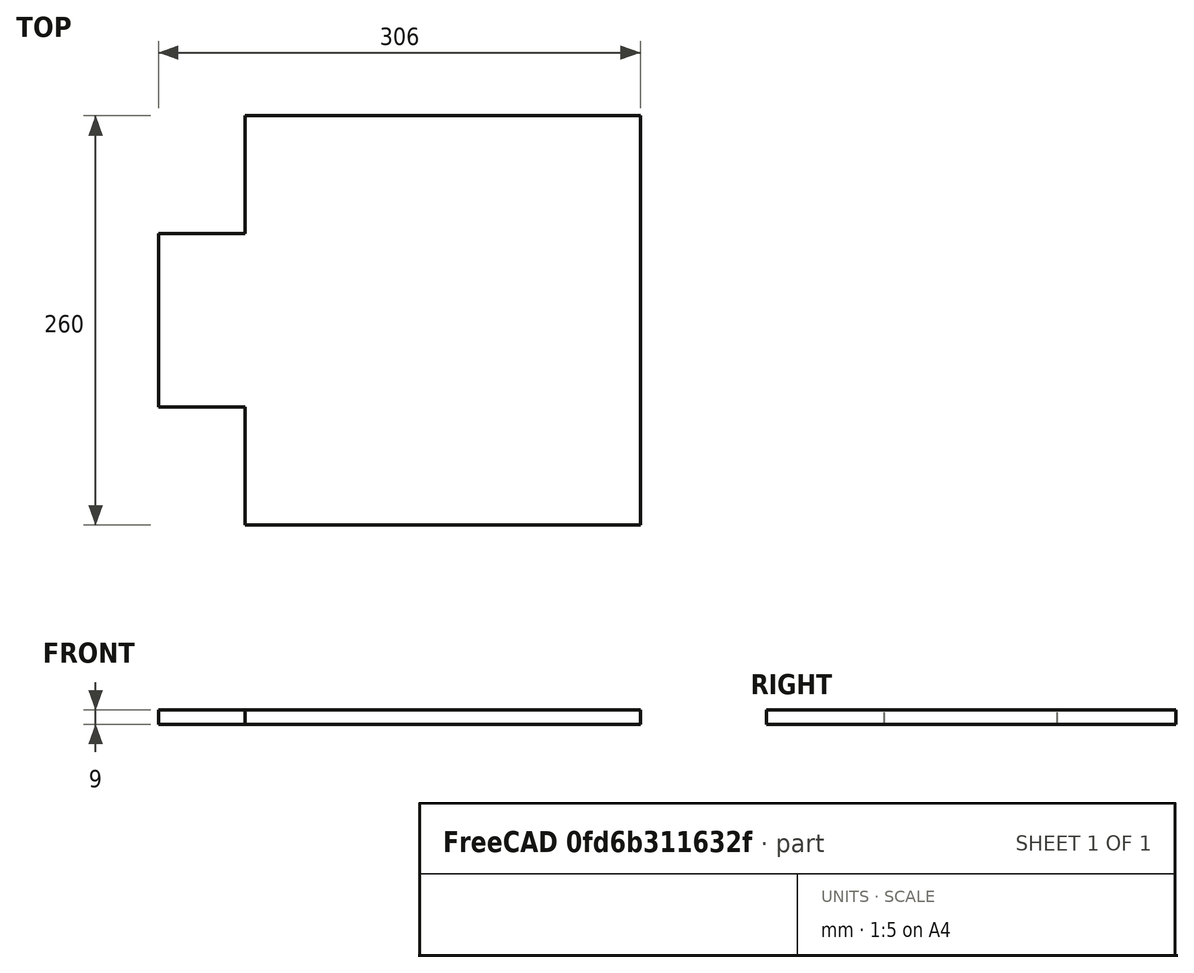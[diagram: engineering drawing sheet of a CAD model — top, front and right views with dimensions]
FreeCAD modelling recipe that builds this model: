
FCSTD DOCUMENT  (FreeCAD 0.16RUnknown)
Label: plaque_ar
License: All rights reserved
LicenseURL: http://en.wikipedia.org/wiki/All_rights_reserved
objects: App::FeaturePython×6, App::DocumentObjectGroup×4, Drawing::FeatureViewPart×4, Part::Plane×3, Drawing::FeatureViewPython×3, Part::Fuse×1, Part::Cut×1, Part::FeaturePython×1, Part::Extrusion×1, Drawing::FeaturePage×1
note: 7 computed .brp shape members not serialized (recipe doc carries the construction recipe); baked Part::Feature solids carry a one-line shape summary decoded from their .brp

FEATURE [Part::Plane] square
  Length = 306
  Placement = pos=(20,-130,0) rot=(0,0,1;0rad)
  Width = 260
FEATURE [Part::Plane] square001
  Length = 75
  Placement = pos=(0,55,0) rot=(0,0,1;0rad)
  Width = 75
FEATURE [Part::Plane] square002
  Length = 75
  Placement = pos=(0,-130,0) rot=(0,0,1;0rad)
  Width = 75
FEATURE [Part::Fuse] union
  Base = -> square001
  Tool = -> square002
FEATURE [Part::Cut] difference
  Base = -> square
  Tool = -> union
FEATURE [Part::FeaturePython] RefineLinearExtrude  # WARN: FeaturePython — macro-defined, semantics opaque (R4)
  Base = -> difference
FEATURE [Part::Extrusion] LinearExtrude
  Base = -> RefineLinearExtrude
  Dir = (0,0,9)
  Solid = true
FEATURE [App::FeaturePython] Dimension  # Draft dimension (typed FeaturePython)
  Dimline = (332,0,0)
  Direction = (0,0,0)
  Distance = 260
  End = (326,-130,0)
  Normal = (0,0,1)
  Start = (326,130,0)
FEATURE [App::FeaturePython] Dimension001  # Draft dimension (typed FeaturePython)
  Dimline = (0,-136,0)
  Direction = (0,0,0)
  Distance = 306
  End = (326,-130,0)
  Normal = (0,0,1)
  Start = (20,-130,0)
FEATURE [App::DocumentObjectGroup] Groupe001  label="XY"
  Group = -> [Dimension,Dimension001]
FEATURE [App::FeaturePython] Dimension002  # Draft dimension (typed FeaturePython)
  Dimline = (0,0,15)
  Direction = (0,0,0)
  Distance = 55
  End = (75,0,9)
  Normal = (0,-1,-1.19209e-07)
  Start = (20,0,9)
FEATURE [App::FeaturePython] Dimension003  # Draft dimension (typed FeaturePython)
  Dimline = (0,0,15)
  Direction = (0,0,0)
  Distance = 251
  End = (326,0,0)
  Normal = (0,-1,-1.19209e-07)
  Start = (75,0,0)
FEATURE [App::DocumentObjectGroup] Groupe002  label="XZ"
  Group = -> [Dimension002,Dimension003]
FEATURE [App::FeaturePython] Dimension004  # Draft dimension (typed FeaturePython)
  Dimline = (0,0,15)
  Direction = (0,0,0)
  Distance = 75
  End = (0,55,9)
  Normal = (-1,0,0)
  Start = (0,130,9)
FEATURE [App::FeaturePython] Dimension005  # Draft dimension (typed FeaturePython)
  Dimline = (0,0,15)
  Direction = (0,0,0)
  Distance = 110
  End = (0,-55,9)
  Normal = (-1,0,0)
  Start = (0,55,9)
FEATURE [App::DocumentObjectGroup] Groupe003  label="YZ"
  Group = -> [Dimension004,Dimension005]
FEATURE [App::DocumentObjectGroup] Groupe  label="Dimmensions"
  Group = -> [Groupe001,Groupe002,Groupe003]
FEATURE [Drawing::FeatureViewPython] ViewGroupe001  # drawing view (typed FeaturePython)
  Direction = (0,0,0)
  FillStyle = 0
  FontSize = 12
  LineStyle = 0
  LineWidth = 0.35
  Rotation = 90
  Scale = 0.38
  Source = -> Groupe001
  ViewResult = <blob: 2051 chars omitted>
  Visible = true
  X = 150
  Y = 71.79
FEATURE [Drawing::FeatureViewPython] ViewGroupe002  # drawing view (typed FeaturePython)
  Direction = (0,0,0)
  FillStyle = 0
  FontSize = 12
  LineStyle = 0
  LineWidth = 0.35
  Rotation = 90
  Scale = 0.38
  Source = -> Groupe002
  ViewResult = <blob: 2024 chars omitted>
  Visible = true
  X = 44.5
  Y = 71.79
FEATURE [Drawing::FeatureViewPython] ViewGroupe003  # drawing view (typed FeaturePython)
  Direction = (0,0,0)
  FillStyle = 0
  FontSize = 12
  LineStyle = 0
  LineWidth = 0.35
  Rotation = -90
  Scale = 0.38
  Source = -> Groupe003
  ViewResult = <g id="ViewGroupe003" transform="rotate(-90.0,150.0,44.33) translate(150.0,44.33) scale(0.38,-0.38)"><path d="M 0.0 130.0 L 0.0 130.0 L 0.0 55.0 L 0.0 55.0" fill="none" stroke="#000000" stroke-width="0.921052631579 px" style="stroke-width:0.921052631579;stroke-miterlimit:4;stroke-dasharray:none" freecad:basepoint1="0.0 130.0" freecad:basepoint2="0.0 55.0" freecad:dimpoint="0.0 130.0"/>\n<path transform="rotate(-90.0,0.0,130.0) translate(0.0,130.0) scale(0.666666666667,0.666666666667)" freecad:skip="1" fill="#000000" stroke="none" style="stroke-miterlimit:4;stroke-dasharray:none" d="M 0 0 L 4 1 L 4 -1 Z"/>\n<path transform="rotate(90.0,0.0,55.0) translate(0.0,55.0) scale(0.666666666667,0.666666666667)" freecad:skip="1" fill="#000000" stroke="none" style="stroke-miterlimit:4;stroke-dasharray:none" d="M 0 0 L 4 1 L 4 -1 Z"/>\n<text fill="#000000" font-size="15.7894736842" style="text-anchor:middle;text-align:center;font-family:" transform="rotate(-90.0,0.0,92.5) translate(0.0,92.5) scale(1,-1) " freecad:skip="1">\n75,00 </text>\n<path d="M 0.0 55.0 L 0.0 55.0 L 0.0 -55.0 L 0.0 -55.0" fill="none" stroke="#000000" stroke-width="0.921052631579 px" style="stroke-width:0.921052631579;stroke-miterlimit:4;stroke-dasharray:none" freecad:basepoint1="0.0 55.0" freecad:basepoint2="0.0 -55.0" freecad:dimpoint="0.0 55.0"/>\n<path transform="rotate(-90.0,0.0,55.0) translate(0.0,55.0) scale(0.666666666667,0.666666666667)" freecad:skip="1" fill="#000000" stroke="none" style="stroke-miterlimit:4;stroke-dasharray:none" d="M 0 0 L 4 1 L 4 -1 Z"/>\n<path transform="rotate(90.0,0.0,-55.0) translate(0.0,-55.0) scale(0.666666666667,0.666666666667)" freecad:skip="1" fill="#000000" stroke="none" style="stroke-miterlimit:4;stroke-dasharray:none" d="M 0 0 L 4 1 L 4 -1 Z"/>\n<text fill="#000000" font-size="15.7894736842" style="text-anchor:middle;text-align:center;font-family:" transform="rotate(-90.0,0.0,0.0) translate(0.0,0.0) scale(1,-1) " freecad:skip="1">\n110,00 </text>\n</g>
  Visible = true
  X = 150
  Y = 44.33
FEATURE [Drawing::FeatureViewPart] Ortho  label="Ortho_0_0"
  Direction = (1,0,0)
  HiddenWidth = 0.15
  LineWidth = 0.35
  Rotation = -90
  Scale = 0.38
  ShowHiddenLines = true
  ShowSmoothLines = false
  Source = -> LinearExtrude
  Tolerance = 0.05
  ViewResult = <g id="Ortho_0_0"\n   transform="rotate(-90,150,46.33) translate(150,46.33) scale(0.38,0.38)"\n  >\n<g   stroke="rgb(0, 0, 0)"\n   stroke-width="0.394737"\n   stroke-linecap="butt"\n   stroke-linejoin="miter"\n   stroke-dasharray="0.2,0.1"\n   fill="none"\n   transform="scale(1,-1)"\n  >\n<path id= "1" d=" M 0 55 L 9 55 " />\n<path id= "2" d=" M 0 -55 L 9 -55 " />\n<path id= "3" d=" M 0 55 L 0 -55 " />\n<path id= "4" d=" M 9 55 L 9 -55 " />\n<path id= "5" d=" M 0 -55 L 9 -55 " />\n<path id= "6" d=" M 0 -130 L 9 -130 " />\n<path id= "7" d=" M 0 -55 L 0 -130 " />\n<path id= "8" d=" M 9 -55 L 9 -130 " />\n<path id= "9" d=" M 0 130 L 9 130 " />\n<path id= "10" d=" M 0 55 L 9 55 " />\n<path id= "11" d=" M 0 130 L 0 55 " />\n<path id= "12" d=" M 9 130 L 9 55 " />\n</g>\n<g   stroke="rgb(0, 0, 0)"\n   stroke-width="0.921053"\n   stroke-linecap="butt"\n   stroke-linejoin="miter"\n   fill="none"\n   transform="scale(1,-1)"\n  >\n<path id= "1" d=" M 0 -130 L 9 -130 " />\n<path id= "2" d=" M 0 130 L 9 130 " />\n<path id= "3" d=" M 0 130 L 0 -130 " />\n<path id= "4" d=" M 9 130 L 9 -130 " />\n</g>\n</g>
  Visible = true
  X = 150
  Y = 46.33
FEATURE [Drawing::FeatureViewPart] Ortho001  label="Ortho_0_-1"
  Direction = (0,0,1)
  HiddenWidth = 0.15
  LineWidth = 0.35
  Rotation = 90
  Scale = 0.38
  ShowHiddenLines = false
  ShowSmoothLines = false
  Source = -> LinearExtrude
  Tolerance = 0.05
  ViewResult = <g id="Ortho_0_-1"\n   transform="rotate(90,150,71.79) translate(150,71.79) scale(0.38,0.38)"\n  >\n<g   stroke="rgb(0, 0, 0)"\n   stroke-width="0.921053"\n   stroke-linecap="butt"\n   stroke-linejoin="miter"\n   fill="none"\n   transform="scale(1,-1)"\n  >\n<path id= "1" d=" M 20 -55 L 20 55 " />\n<path id= "2" d=" M 20 55 L 75 55 " />\n<path id= "3" d=" M 75 55 L 75 130 " />\n<path id= "4" d=" M 75 130 L 326 130 " />\n<path id= "5" d=" M 326 -130 L 326 130 " />\n<path id= "6" d=" M 75 -130 L 326 -130 " />\n<path id= "7" d=" M 75 -130 L 75 -55 " />\n<path id= "8" d=" M 20 -55 L 75 -55 " />\n</g>\n</g>
  Visible = true
  X = 150
  Y = 71.79
FEATURE [Drawing::FeatureViewPart] Ortho002  label="Ortho_-1_0"
  Direction = (0,1,0)
  HiddenWidth = 0.15
  LineWidth = 0.35
  Rotation = 180
  Scale = 0.38
  ShowHiddenLines = false
  ShowSmoothLines = false
  Source = -> LinearExtrude
  Tolerance = 0.05
  ViewResult = <g id="Ortho_-1_0"\n   transform="rotate(180,46.5,71.79) translate(46.5,71.79) scale(0.38,0.38)"\n  >\n<g   stroke="rgb(0, 0, 0)"\n   stroke-width="0.921053"\n   stroke-linecap="butt"\n   stroke-linejoin="miter"\n   fill="none"\n   transform="scale(1,-1)"\n  >\n<path id= "1" d=" M 0 20 L 9 20 " />\n<path id= "2" d=" M 0 20 L 0 75 " />\n<path id= "3" d=" M 9 20 L 9 75 " />\n<path id= "4" d=" M 0 75 L 9 75 " />\n<path id= "5" d=" M 0 326 L 9 326 " />\n<path id= "6" d=" M 0 75 L 0 326 " />\n<path id= "7" d=" M 9 75 L 9 326 " />\n</g>\n</g>
  Visible = true
  X = 46.5
  Y = 71.79
FEATURE [Drawing::FeatureViewPart] Ortho003  label="Ortho_1_-1"
  Direction = (0.57735,-0.57735,0.57735)
  HiddenWidth = 0.15
  LineWidth = 0.35
  Rotation = 60
  Scale = 0.38
  ShowHiddenLines = false
  ShowSmoothLines = false
  Source = -> LinearExtrude
  Tolerance = 0.05
  ViewResult = <g id="Ortho_1_-1"\n   transform="rotate(60,248.5,111.559) translate(248.5,111.559) scale(0.38,0.38)"\n  >\n<g   stroke="rgb(0, 0, 0)"\n   stroke-width="0.921053"\n   stroke-linecap="butt"\n   stroke-linejoin="miter"\n   fill="none"\n   transform="scale(1,-1)"\n  >\n<path id= "1" d=" M 14.1421 -36.7423 L 7.77817 -33.0681 " />\n<path id= "2" d=" M 7.77817 -33.0681 L 7.77817 56.7465 " />\n<path id= "3" d=" M 7.77817 56.7465 L 46.669 79.2002 " />\n<path id= "4" d=" M 46.669 79.2002 L 46.669 140.437 " />\n<path id= "5" d=" M 230.517 239.233 L 224.153 242.908 " />\n<path id= "6" d=" M 46.669 140.437 L 224.153 242.908 " />\n<path id= "7" d=" M 230.517 26.9444 L 224.153 30.6186 " />\n<path id= "8" d=" M 230.517 26.9444 L 230.517 239.233 " />\n<path id= "9" d=" M 224.153 30.6186 L 224.153 242.908 " />\n<path id= "10" d=" M 53.033 -75.5259 L 46.669 -71.8517 " />\n<path id= "11" d=" M 53.033 -75.5259 L 230.517 26.9444 " />\n<path id= "12" d=" M 46.669 -71.8517 L 224.153 30.6186 " />\n<path id= "13" d=" M 46.669 -71.8517 L 46.669 -10.6145 " />\n<path id= "14" d=" M 14.1421 -36.7423 L 46.669 -17.9629 " />\n<path id= "15" d=" M 7.77817 -33.0681 L 46.669 -10.6145 " />\n</g>\n</g>
  Visible = true
  X = 248.5
  Y = 111.559
FEATURE [Drawing::FeaturePage] Page
  EditableTexts = AUTHOR NAME | CREATION DATE | SUPERVISOR NAME | CHECK DATE | 0,38 | WEIGHT | NUMBER | SHEET | Caisse | Arrière
  Group = -> [ViewGroupe001,ViewGroupe002,ViewGroupe003,Ortho,Ortho001,Ortho002,Ortho003]
